# Revit family: 54-3132-001 DN1400-1800
name_source: partatom
category: Pipe Accessories
units: mm (PartAtom-declared; Revit-internal decimal feet)

## family parameters
Always vertical = No
Cut with Voids When Loaded = No
Part Type = Valve - Breaks Into
Round Connector Dimension = Use Diameter
Shared = No
Work Plane-Based = No

## types (19) — shared parameters
1 = 1 mm  [stored 0.00328084 ft]
10 = 10 mm  [stored 0.0328084 ft]
54-1400-31-0303100 = DN1400_ PN10_ CTC
54-1400-31-0304100 = DN1400_ PN10_ CTC
54-1400-31-1303100 = DN1400_ PN16_ CTC
54-1400-31-1304100 = DN1400_ PN16_ CTC
54-1400-32-0303100 = DN1400_ PN10_ CTO
54-1400-32-1303100 = DN1400_ PN16_ CTO
54-1400-32-1304100 = DN1400_ PN16_ CTO
54-1500-31-0304100 = DN1500_ PN10_ CTC
54-1500-31-1304100 = DN1500_ PN16_ CTC
54-1600-31-0303100 = DN1600_ PN10_ CTC
54-1600-31-0304100 = DN1600_ PN10_ CTC
54-1600-31-1303100 = DN1600_ PN16_ CTC
54-1600-31-1304100 = DN1600_ PN16_ CTC
54-1600-32-0303100 = DN1600_ PN10_ CTO
54-1600-32-1303100 = DN1600_ PN16_ CTO
54-1800-31-0304100 = DN1800_ PN10_ CTC
54-1800-31-1304100 = DN1800_ PN16_ CTC
54-1800-32-0304100 = DN1800_ PN10_ CTO
54-1800-32-1304100 = DN1800_ PN16_ CTO
Bypass_W = 82 mm
Bypass_dis = 60 mm
Description_ = AVK METAL SEAT GATE VALVE, FLANGED, PN 10/16
H = 782 mm
Raised_dis = 5 mm  [stored 0.0164042 ft]
Rib_H1 = 300 mm
Search_table = 54-3132-001 DN1400-1800
URL product pages = https://www.avkvalves.com
sweep = 6 mm  [stored 0.019685 ft]
zero-valued in all types: Default Elevation

## per-type parameters (varying)
- 54-1400-31-0303100: ACtuator_T=33.12 mm  [stored 0.108661 ft]; ADN=1400 mm; Actuator_FLR=150 mm; Actuator_angle=133.41 mm; Actuator_dim1=90 mm; Actuator_dim2=54 mm  [stored 0.177165 ft]; BP_centre=31 mm  [stored 0.101706 ft]; Body_H=1435 mm; Body_L=1564.8 mm; Body_T=692.5 mm; Body_W=648 mm; Body_rib_T=18.4 mm  [stored 0.0603675 ft]; Bonnet_FL_L=1956 mm; Bonnet_FL_T=87.4 mm; Bonnet_FL_W=864 mm; Bonnet_dim1=312.96 mm; Bonnet_dim2=226.8 mm; Bonnet_dim3=2468.2 mm; Bonnet_fillet=72 mm; Bore=700 mm; Bypass_Arc=85 mm; Bypass_Location=220 mm; Bypass_R=62 mm; Bypass_R1=124 mm; Bypass_T=25 mm  [stored 0.082021 ft]; Bypass_shaft=150 mm; Cut_dis=43.7 mm  [stored 0.143373 ft]; DN=1400 mm; F=60 mm; F1=27 mm  [stored 0.0885827 ft]; F2=166 mm; FL_T=46 mm  [stored 0.150919 ft]; Fillet=216 mm; H1=2870 mm; H2=885 mm; L=876 mm; OD=1770 mm; OD1=1770 mm; PN=10 mm  [stored 0.0328084 ft]; Raised_dia=1530 mm; Rib_Actual=978 mm; Rib_H=1148 mm; Rib_H2=950 mm; Rib_H3=1200 mm; Rib_H4=1310 mm; Rib_L=880.2 mm; Rib_W=388.8 mm; Stem_dim=75 mm; W=1956 mm; W1=897 mm; W_half=1059 mm; bottom_rib=885 mm; stem_dim=55.33 mm; stem_dim1=97.5 mm; wedge_dim1=712.8 mm
- 54-1400-31-0304100: ACtuator_T=33.12 mm  [stored 0.108661 ft]; ADN=1400 mm; Actuator_FLR=175 mm; Actuator_angle=133.41 mm; Actuator_dim1=105 mm; Actuator_dim2=63 mm; BP_centre=31 mm  [stored 0.101706 ft]; Body_H=1435 mm; Body_L=1564.8 mm; Body_T=692.5 mm; Body_W=648 mm; Body_rib_T=18.4 mm  [stored 0.0603675 ft]; Bonnet_FL_L=1956 mm; Bonnet_FL_T=87.4 mm; Bonnet_FL_W=864 mm; Bonnet_dim1=312.96 mm; Bonnet_dim2=226.8 mm; Bonnet_dim3=2468.2 mm; Bonnet_fillet=72 mm; Bore=700.05 mm; Bypass_Arc=85 mm; Bypass_Location=220 mm; Bypass_R=62 mm; Bypass_R1=124 mm; Bypass_T=25 mm  [stored 0.082021 ft]; Bypass_shaft=150 mm; Cut_dis=43.7 mm  [stored 0.143373 ft]; DN=1400.1 mm; F=70 mm; F1=31.5 mm  [stored 0.103346 ft]; F2=202 mm; FL_T=46 mm  [stored 0.150919 ft]; Fillet=216 mm; H1=2870 mm; H2=885 mm; L=876 mm; OD=1770 mm; OD1=1770 mm; PN=10 mm  [stored 0.0328084 ft]; Raised_dia=1530 mm; Rib_Actual=978 mm; Rib_H=1148 mm; Rib_H2=950 mm; Rib_H3=1200 mm; Rib_H4=1310 mm; Rib_L=880.2 mm; Rib_W=388.8 mm; Stem_dim=87.5 mm; W=1956 mm; W1=897 mm; W_half=1059 mm; bottom_rib=885 mm; stem_dim=67.33 mm; stem_dim1=113.75 mm; wedge_dim1=712.8 mm
- 54-1400-31-1303100: ACtuator_T=43.2 mm  [stored 0.141732 ft]; ADN=1400 mm; Actuator_FLR=150 mm; Actuator_angle=133.41 mm; Actuator_dim1=90 mm; Actuator_dim2=54 mm  [stored 0.177165 ft]; BP_centre=31 mm  [stored 0.101706 ft]; Body_H=1435 mm; Body_L=1564.8 mm; Body_T=692.5 mm; Body_W=648 mm; Body_rib_T=24 mm  [stored 0.0787402 ft]; Bonnet_FL_L=1956 mm; Bonnet_FL_T=114 mm; Bonnet_FL_W=864 mm; Bonnet_dim1=312.96 mm; Bonnet_dim2=226.8 mm; Bonnet_dim3=2468.2 mm; Bonnet_fillet=72 mm; Bore=700.06 mm; Bypass_Arc=85 mm; Bypass_Location=220 mm; Bypass_R=62 mm; Bypass_R1=124 mm; Bypass_T=25 mm  [stored 0.082021 ft]; Bypass_shaft=150 mm; Cut_dis=57 mm; DN=1400.11 mm; F=60 mm; F1=27 mm  [stored 0.0885827 ft]; F2=166 mm; FL_T=60 mm; Fillet=216 mm; H1=2870 mm; H2=885 mm; L=876 mm; OD=1770 mm; OD1=1770 mm; PN=16 mm  [stored 0.0524934 ft]; Raised_dia=1530 mm; Rib_Actual=978 mm; Rib_H=1148 mm; Rib_H2=950 mm; Rib_H3=1200 mm; Rib_H4=1310 mm; Rib_L=880.2 mm; Rib_W=388.8 mm; Stem_dim=75 mm; W=1956 mm; W1=897 mm; W_half=1059 mm; bottom_rib=885 mm; stem_dim=55.33 mm; stem_dim1=97.5 mm; wedge_dim1=712.8 mm
- 54-1400-31-1304100: ACtuator_T=43.2 mm  [stored 0.141732 ft]; ADN=1400 mm; Actuator_FLR=175 mm; Actuator_angle=133.41 mm; Actuator_dim1=105 mm; Actuator_dim2=63 mm; BP_centre=31 mm  [stored 0.101706 ft]; Body_H=1435 mm; Body_L=1564.8 mm; Body_T=692.5 mm; Body_W=648 mm; Body_rib_T=24 mm  [stored 0.0787402 ft]; Bonnet_FL_L=1956 mm; Bonnet_FL_T=114 mm; Bonnet_FL_W=864 mm; Bonnet_dim1=312.96 mm; Bonnet_dim2=226.8 mm; Bonnet_dim3=2468.2 mm; Bonnet_fillet=72 mm; Bore=700.06 mm; Bypass_Arc=85 mm; Bypass_Location=220 mm; Bypass_R=62 mm; Bypass_R1=124 mm; Bypass_T=25 mm  [stored 0.082021 ft]; Bypass_shaft=150 mm; Cut_dis=57 mm; DN=1400.12 mm; F=70 mm; F1=31.5 mm  [stored 0.103346 ft]; F2=202 mm; FL_T=60 mm; Fillet=216 mm; H1=2870 mm; H2=885 mm; L=876 mm; OD=1770 mm; OD1=1770 mm; PN=16 mm  [stored 0.0524934 ft]; Raised_dia=1530 mm; Rib_Actual=978 mm; Rib_H=1148 mm; Rib_H2=950 mm; Rib_H3=1200 mm; Rib_H4=1310 mm; Rib_L=880.2 mm; Rib_W=388.8 mm; Stem_dim=87.5 mm; W=1956 mm; W1=897 mm; W_half=1059 mm; bottom_rib=885 mm; stem_dim=67.33 mm; stem_dim1=113.75 mm; wedge_dim1=712.8 mm
- 54-1400-32-0303100: ACtuator_T=33.12 mm  [stored 0.108661 ft]; ADN=1400 mm; Actuator_FLR=150 mm; Actuator_angle=133.41 mm; Actuator_dim1=90 mm; Actuator_dim2=54 mm  [stored 0.177165 ft]; BP_centre=31 mm  [stored 0.101706 ft]; Body_H=1435 mm; Body_L=1564.8 mm; Body_T=692.5 mm; Body_W=648 mm; Body_rib_T=18.4 mm  [stored 0.0603675 ft]; Bonnet_FL_L=1956 mm; Bonnet_FL_T=87.4 mm; Bonnet_FL_W=864 mm; Bonnet_dim1=312.96 mm; Bonnet_dim2=226.8 mm; Bonnet_dim3=2468.2 mm; Bonnet_fillet=72 mm; Bore=700.07 mm; Bypass_Arc=85 mm; Bypass_Location=220 mm; Bypass_R=62 mm; Bypass_R1=124 mm; Bypass_T=25 mm  [stored 0.082021 ft]; Bypass_shaft=150 mm; Cut_dis=43.7 mm  [stored 0.143373 ft]; DN=1400.13 mm; F=60 mm; F1=27 mm  [stored 0.0885827 ft]; F2=166 mm; FL_T=46 mm  [stored 0.150919 ft]; Fillet=216 mm; H1=2870 mm; H2=885 mm; L=876 mm; OD=1770 mm; OD1=1770 mm; PN=10 mm  [stored 0.0328084 ft]; Raised_dia=1530 mm; Rib_Actual=978 mm; Rib_H=1148 mm; Rib_H2=950 mm; Rib_H3=1200 mm; Rib_H4=1310 mm; Rib_L=880.2 mm; Rib_W=388.8 mm; Stem_dim=75 mm; W=1956 mm; W1=897 mm; W_half=1059 mm; bottom_rib=885 mm; stem_dim=55.33 mm; stem_dim1=97.5 mm; wedge_dim1=712.8 mm
- 54-1400-32-1303100: ACtuator_T=43.2 mm  [stored 0.141732 ft]; ADN=1400 mm; Actuator_FLR=150 mm; Actuator_angle=133.41 mm; Actuator_dim1=90 mm; Actuator_dim2=54 mm  [stored 0.177165 ft]; BP_centre=31 mm  [stored 0.101706 ft]; Body_H=1435 mm; Body_L=1564.8 mm; Body_T=692.5 mm; Body_W=648 mm; Body_rib_T=24 mm  [stored 0.0787402 ft]; Bonnet_FL_L=1956 mm; Bonnet_FL_T=114 mm; Bonnet_FL_W=864 mm; Bonnet_dim1=312.96 mm; Bonnet_dim2=226.8 mm; Bonnet_dim3=2468.2 mm; Bonnet_fillet=72 mm; Bore=700.07 mm; Bypass_Arc=85 mm; Bypass_Location=220 mm; Bypass_R=62 mm; Bypass_R1=124 mm; Bypass_T=25 mm  [stored 0.082021 ft]; Bypass_shaft=150 mm; Cut_dis=57 mm; DN=1400.14 mm; F=60 mm; F1=27 mm  [stored 0.0885827 ft]; F2=166 mm; FL_T=60 mm; Fillet=216 mm; H1=2870 mm; H2=885 mm; L=876 mm; OD=1770 mm; OD1=1770 mm; PN=16 mm  [stored 0.0524934 ft]; Raised_dia=1530 mm; Rib_Actual=978 mm; Rib_H=1148 mm; Rib_H2=950 mm; Rib_H3=1200 mm; Rib_H4=1310 mm; Rib_L=880.2 mm; Rib_W=388.8 mm; Stem_dim=75 mm; W=1956 mm; W1=897 mm; W_half=1059 mm; bottom_rib=885 mm; stem_dim=55.33 mm; stem_dim1=97.5 mm; wedge_dim1=712.8 mm
- 54-1400-32-1304100: ACtuator_T=43.2 mm  [stored 0.141732 ft]; ADN=1400 mm; Actuator_FLR=175 mm; Actuator_angle=133.41 mm; Actuator_dim1=105 mm; Actuator_dim2=63 mm; BP_centre=31 mm  [stored 0.101706 ft]; Body_H=1435 mm; Body_L=1564.8 mm; Body_T=692.5 mm; Body_W=648 mm; Body_rib_T=24 mm  [stored 0.0787402 ft]; Bonnet_FL_L=1956 mm; Bonnet_FL_T=114 mm; Bonnet_FL_W=864 mm; Bonnet_dim1=312.96 mm; Bonnet_dim2=226.8 mm; Bonnet_dim3=2468.2 mm; Bonnet_fillet=72 mm; Bore=700.08 mm; Bypass_Arc=85 mm; Bypass_Location=220 mm; Bypass_R=62 mm; Bypass_R1=124 mm; Bypass_T=25 mm  [stored 0.082021 ft]; Bypass_shaft=150 mm; Cut_dis=57 mm; DN=1400.15 mm; F=70 mm; F1=31.5 mm  [stored 0.103346 ft]; F2=202 mm; FL_T=60 mm; Fillet=216 mm; H1=2870 mm; H2=885 mm; L=876 mm; OD=1770 mm; OD1=1770 mm; PN=16 mm  [stored 0.0524934 ft]; Raised_dia=1530 mm; Rib_Actual=978 mm; Rib_H=1148 mm; Rib_H2=950 mm; Rib_H3=1200 mm; Rib_H4=1310 mm; Rib_L=880.2 mm; Rib_W=388.8 mm; Stem_dim=87.5 mm; W=1956 mm; W1=897 mm; W_half=1059 mm; bottom_rib=885 mm; stem_dim=67.33 mm; stem_dim1=113.75 mm; wedge_dim1=712.8 mm
- 54-1500-31-0304100: ACtuator_T=34.2 mm  [stored 0.112205 ft]; ADN=1500 mm; Actuator_FLR=175 mm; Actuator_angle=141.13 mm; Actuator_dim1=105 mm; Actuator_dim2=63 mm; BP_centre=37.5 mm; Body_H=1584.5 mm; Body_L=1768 mm; Body_T=742.5 mm; Body_W=685.5 mm; Body_rib_T=19 mm  [stored 0.062336 ft]; Bonnet_FL_L=2210 mm; Bonnet_FL_T=90.25 mm; Bonnet_FL_W=914 mm; Bonnet_dim1=353.6 mm; Bonnet_dim2=239.93 mm; Bonnet_dim3=2725.34 mm; Bonnet_fillet=76.17 mm; Bore=750 mm; Bypass_Arc=85 mm; Bypass_Location=220 mm; Bypass_R=75 mm; Bypass_R1=150 mm; Bypass_T=18 mm  [stored 0.0590551 ft]; Bypass_shaft=160 mm; Cut_dis=45.13 mm; DN=1500 mm; F=70 mm; F1=31.5 mm  [stored 0.103346 ft]; F2=205 mm; FL_T=47.5 mm; Fillet=228.5 mm; H1=3169 mm; H2=1016 mm; L=914 mm; OD=2032 mm; OD1=2032 mm; PN=10 mm  [stored 0.0328084 ft]; Raised_dia=1640 mm; Rib_Actual=1105 mm; Rib_H=1267.6 mm; Rib_H2=1200 mm; Rib_H3=1300 mm; Rib_H4=1450 mm; Rib_L=994.5 mm; Rib_W=411.3 mm; Stem_dim=87.5 mm; W=2210 mm; W1=1000 mm; W_half=1210 mm; bottom_rib=1016 mm; stem_dim=68.33 mm; stem_dim1=113.75 mm; wedge_dim1=754.05 mm
- 54-1500-31-1304100: ACtuator_T=45 mm  [stored 0.147638 ft]; ADN=1500 mm; Actuator_FLR=175 mm; Actuator_angle=141.13 mm; Actuator_dim1=105 mm; Actuator_dim2=63 mm; BP_centre=37.5 mm; Body_H=1584.5 mm; Body_L=1768 mm; Body_T=742.5 mm; Body_W=685.5 mm; Body_rib_T=25 mm  [stored 0.082021 ft]; Bonnet_FL_L=2210 mm; Bonnet_FL_T=118.75 mm; Bonnet_FL_W=914 mm; Bonnet_dim1=353.6 mm; Bonnet_dim2=239.93 mm; Bonnet_dim3=2725.34 mm; Bonnet_fillet=76.17 mm; Bore=750.05 mm; Bypass_Arc=85 mm; Bypass_Location=220 mm; Bypass_R=75 mm; Bypass_R1=150 mm; Bypass_T=18 mm  [stored 0.0590551 ft]; Bypass_shaft=160 mm; Cut_dis=59.38 mm; DN=1500.1 mm; F=70 mm; F1=31.5 mm  [stored 0.103346 ft]; F2=205 mm; FL_T=62.5 mm; Fillet=228.5 mm; H1=3169 mm; H2=1016 mm; L=914 mm; OD=2032 mm; OD1=2032 mm; PN=16 mm  [stored 0.0524934 ft]; Raised_dia=1640 mm; Rib_Actual=1105 mm; Rib_H=1267.6 mm; Rib_H2=1200 mm; Rib_H3=1300 mm; Rib_H4=1450 mm; Rib_L=994.5 mm; Rib_W=411.3 mm; Stem_dim=87.5 mm; W=2210 mm; W1=1000 mm; W_half=1210 mm; bottom_rib=1016 mm; stem_dim=68.33 mm; stem_dim1=113.75 mm; wedge_dim1=754.05 mm
- 54-1600-31-0303100: ACtuator_T=35.28 mm  [stored 0.115748 ft]; ADN=1600 mm; Actuator_FLR=150 mm; Actuator_angle=141.13 mm; Actuator_dim1=90 mm; Actuator_dim2=54 mm  [stored 0.177165 ft]; BP_centre=40 mm  [stored 0.131234 ft]; Body_H=1645.5 mm; Body_L=1832 mm; Body_T=792.5 mm; Body_W=685.5 mm; Body_rib_T=19.6 mm  [stored 0.0643045 ft]; Bonnet_FL_L=2290 mm; Bonnet_FL_T=93.1 mm; Bonnet_FL_W=914 mm; Bonnet_dim1=366.4 mm; Bonnet_dim2=239.93 mm; Bonnet_dim3=2830.26 mm; Bonnet_fillet=76.17 mm; Bore=800 mm; Bypass_Arc=100 mm; Bypass_Location=259 mm; Bypass_R=80 mm; Bypass_R1=160 mm; Bypass_T=35 mm  [stored 0.114829 ft]; Bypass_shaft=170 mm; Cut_dis=46.55 mm  [stored 0.152723 ft]; DN=1600 mm; F=60 mm; F1=27 mm  [stored 0.0885827 ft]; F2=179 mm; FL_T=49 mm  [stored 0.160761 ft]; Fillet=228.5 mm; H1=3291 mm; H2=1060 mm; L=914 mm; OD=2120 mm; OD1=2120 mm; PN=10 mm  [stored 0.0328084 ft]; Raised_dia=1750 mm; Rib_Actual=1145 mm; Rib_H=1316.4 mm; Rib_H2=1100 mm; Rib_H3=1300 mm; Rib_H4=1500 mm; Rib_L=1030.5 mm; Rib_W=411.3 mm; Stem_dim=75 mm; W=2290 mm; W1=1104 mm; W_half=1186 mm; bottom_rib=1060 mm; stem_dim=59.67 mm; stem_dim1=97.5 mm; wedge_dim1=754.05 mm
- 54-1600-31-0304100: ACtuator_T=35.28 mm  [stored 0.115748 ft]; ADN=1600 mm; Actuator_FLR=175 mm; Actuator_angle=141.13 mm; Actuator_dim1=105 mm; Actuator_dim2=63 mm; BP_centre=40 mm  [stored 0.131234 ft]; Body_H=1645.5 mm; Body_L=1832 mm; Body_T=792.5 mm; Body_W=685.5 mm; Body_rib_T=19.6 mm  [stored 0.0643045 ft]; Bonnet_FL_L=2290 mm; Bonnet_FL_T=93.1 mm; Bonnet_FL_W=914 mm; Bonnet_dim1=366.4 mm; Bonnet_dim2=239.93 mm; Bonnet_dim3=2830.26 mm; Bonnet_fillet=76.17 mm; Bore=800.05 mm; Bypass_Arc=100 mm; Bypass_Location=259 mm; Bypass_R=80 mm; Bypass_R1=160 mm; Bypass_T=35 mm  [stored 0.114829 ft]; Bypass_shaft=170 mm; Cut_dis=46.55 mm  [stored 0.152723 ft]; DN=1600.1 mm; F=70 mm; F1=31.5 mm  [stored 0.103346 ft]; F2=205 mm; FL_T=49 mm  [stored 0.160761 ft]; Fillet=228.5 mm; H1=3291 mm; H2=1060 mm; L=914 mm; OD=2120 mm; OD1=2120 mm; PN=10 mm  [stored 0.0328084 ft]; Raised_dia=1750 mm; Rib_Actual=1145 mm; Rib_H=1316.4 mm; Rib_H2=1100 mm; Rib_H3=1300 mm; Rib_H4=1500 mm; Rib_L=1030.5 mm; Rib_W=411.3 mm; Stem_dim=87.5 mm; W=2290 mm; W1=1104 mm; W_half=1186 mm; bottom_rib=1060 mm; stem_dim=68.33 mm; stem_dim1=113.75 mm; wedge_dim1=754.05 mm
- 54-1600-31-1303100: ACtuator_T=46.8 mm  [stored 0.153543 ft]; ADN=1600 mm; Actuator_FLR=150 mm; Actuator_angle=141.13 mm; Actuator_dim1=90 mm; Actuator_dim2=54 mm  [stored 0.177165 ft]; BP_centre=40 mm  [stored 0.131234 ft]; Body_H=1645.5 mm; Body_L=1832 mm; Body_T=792.5 mm; Body_W=685.5 mm; Body_rib_T=26 mm; Bonnet_FL_L=2290 mm; Bonnet_FL_T=123.5 mm; Bonnet_FL_W=914 mm; Bonnet_dim1=366.4 mm; Bonnet_dim2=239.93 mm; Bonnet_dim3=2830.26 mm; Bonnet_fillet=76.17 mm; Bore=800.06 mm; Bypass_Arc=100 mm; Bypass_Location=259 mm; Bypass_R=80 mm; Bypass_R1=160 mm; Bypass_T=35 mm  [stored 0.114829 ft]; Bypass_shaft=170 mm; Cut_dis=61.75 mm; DN=1600.11 mm; F=60 mm; F1=27 mm  [stored 0.0885827 ft]; F2=179 mm; FL_T=65 mm; Fillet=228.5 mm; H1=3291 mm; H2=1060 mm; L=914 mm; OD=2120 mm; OD1=2120 mm; PN=16 mm  [stored 0.0524934 ft]; Raised_dia=1750 mm; Rib_Actual=1145 mm; Rib_H=1316.4 mm; Rib_H2=1100 mm; Rib_H3=1300 mm; Rib_H4=1500 mm; Rib_L=1030.5 mm; Rib_W=411.3 mm; Stem_dim=75 mm; W=2290 mm; W1=1104 mm; W_half=1186 mm; bottom_rib=1060 mm; stem_dim=59.67 mm; stem_dim1=97.5 mm; wedge_dim1=754.05 mm
- 54-1600-31-1304100: ACtuator_T=46.8 mm  [stored 0.153543 ft]; ADN=1600 mm; Actuator_FLR=175 mm; Actuator_angle=141.13 mm; Actuator_dim1=105 mm; Actuator_dim2=63 mm; BP_centre=40 mm  [stored 0.131234 ft]; Body_H=1645.5 mm; Body_L=1832 mm; Body_T=792.5 mm; Body_W=685.5 mm; Body_rib_T=26 mm; Bonnet_FL_L=2290 mm; Bonnet_FL_T=123.5 mm; Bonnet_FL_W=914 mm; Bonnet_dim1=366.4 mm; Bonnet_dim2=239.93 mm; Bonnet_dim3=2830.26 mm; Bonnet_fillet=76.17 mm; Bore=800.06 mm; Bypass_Arc=100 mm; Bypass_Location=259 mm; Bypass_R=80 mm; Bypass_R1=160 mm; Bypass_T=35 mm  [stored 0.114829 ft]; Bypass_shaft=170 mm; Cut_dis=61.75 mm; DN=1600.12 mm; F=70 mm; F1=31.5 mm  [stored 0.103346 ft]; F2=205 mm; FL_T=65 mm; Fillet=228.5 mm; H1=3291 mm; H2=1060 mm; L=914 mm; OD=2120 mm; OD1=2120 mm; PN=16 mm  [stored 0.0524934 ft]; Raised_dia=1750 mm; Rib_Actual=1145 mm; Rib_H=1316.4 mm; Rib_H2=1100 mm; Rib_H3=1300 mm; Rib_H4=1500 mm; Rib_L=1030.5 mm; Rib_W=411.3 mm; Stem_dim=87.5 mm; W=2290 mm; W1=1104 mm; W_half=1186 mm; bottom_rib=1060 mm; stem_dim=68.33 mm; stem_dim1=113.75 mm; wedge_dim1=754.05 mm
- 54-1600-32-0303100: ACtuator_T=35.28 mm  [stored 0.115748 ft]; ADN=1600 mm; Actuator_FLR=150 mm; Actuator_angle=141.13 mm; Actuator_dim1=90 mm; Actuator_dim2=54 mm  [stored 0.177165 ft]; BP_centre=40 mm  [stored 0.131234 ft]; Body_H=1645.5 mm; Body_L=1832 mm; Body_T=792.5 mm; Body_W=685.5 mm; Body_rib_T=19.6 mm  [stored 0.0643045 ft]; Bonnet_FL_L=2290 mm; Bonnet_FL_T=93.1 mm; Bonnet_FL_W=914 mm; Bonnet_dim1=366.4 mm; Bonnet_dim2=239.93 mm; Bonnet_dim3=2830.26 mm; Bonnet_fillet=76.17 mm; Bore=800.07 mm; Bypass_Arc=100 mm; Bypass_Location=259 mm; Bypass_R=80 mm; Bypass_R1=160 mm; Bypass_T=35 mm  [stored 0.114829 ft]; Bypass_shaft=170 mm; Cut_dis=46.55 mm  [stored 0.152723 ft]; DN=1600.13 mm; F=60 mm; F1=27 mm  [stored 0.0885827 ft]; F2=179 mm; FL_T=49 mm  [stored 0.160761 ft]; Fillet=228.5 mm; H1=3291 mm; H2=1060 mm; L=914 mm; OD=2120 mm; OD1=2120 mm; PN=10 mm  [stored 0.0328084 ft]; Raised_dia=1750 mm; Rib_Actual=1145 mm; Rib_H=1316.4 mm; Rib_H2=1100 mm; Rib_H3=1300 mm; Rib_H4=1500 mm; Rib_L=1030.5 mm; Rib_W=411.3 mm; Stem_dim=75 mm; W=2290 mm; W1=1104 mm; W_half=1186 mm; bottom_rib=1060 mm; stem_dim=59.67 mm; stem_dim1=97.5 mm; wedge_dim1=754.05 mm
- 54-1600-32-1303100: ACtuator_T=46.8 mm  [stored 0.153543 ft]; ADN=1600 mm; Actuator_FLR=150 mm; Actuator_angle=141.13 mm; Actuator_dim1=90 mm; Actuator_dim2=54 mm  [stored 0.177165 ft]; BP_centre=40 mm  [stored 0.131234 ft]; Body_H=1645.5 mm; Body_L=1832 mm; Body_T=792.5 mm; Body_W=685.5 mm; Body_rib_T=26 mm; Bonnet_FL_L=2290 mm; Bonnet_FL_T=123.5 mm; Bonnet_FL_W=914 mm; Bonnet_dim1=366.4 mm; Bonnet_dim2=239.93 mm; Bonnet_dim3=2830.26 mm; Bonnet_fillet=76.17 mm; Bore=800.07 mm; Bypass_Arc=100 mm; Bypass_Location=259 mm; Bypass_R=80 mm; Bypass_R1=160 mm; Bypass_T=35 mm  [stored 0.114829 ft]; Bypass_shaft=170 mm; Cut_dis=61.75 mm; DN=1600.14 mm; F=60 mm; F1=27 mm  [stored 0.0885827 ft]; F2=179 mm; FL_T=65 mm; Fillet=228.5 mm; H1=3291 mm; H2=1060 mm; L=914 mm; OD=2120 mm; OD1=2120 mm; PN=16 mm  [stored 0.0524934 ft]; Raised_dia=1750 mm; Rib_Actual=1145 mm; Rib_H=1316.4 mm; Rib_H2=1100 mm; Rib_H3=1300 mm; Rib_H4=1500 mm; Rib_L=1030.5 mm; Rib_W=411.3 mm; Stem_dim=75 mm; W=2290 mm; W1=1104 mm; W_half=1186 mm; bottom_rib=1060 mm; stem_dim=59.67 mm; stem_dim1=97.5 mm; wedge_dim1=754.05 mm
- 54-1800-31-0304100: ACtuator_T=37.44 mm  [stored 0.122835 ft]; ADN=1800 mm; Actuator_FLR=175 mm; Actuator_angle=156.88 mm; Actuator_dim1=105 mm; Actuator_dim2=63 mm; BP_centre=42.5 mm  [stored 0.139436 ft]; Body_H=1829.5 mm; Body_L=1910.4 mm; Body_T=892.5 mm; Body_W=762 mm; Body_rib_T=20.8 mm  [stored 0.0682415 ft]; Bonnet_FL_L=2388 mm; Bonnet_FL_T=98.8 mm; Bonnet_FL_W=1016 mm; Bonnet_dim1=382.08 mm; Bonnet_dim2=266.7 mm; Bonnet_dim3=3146.74 mm; Bonnet_fillet=84.67 mm; Bore=900 mm; Bypass_Arc=105 mm; Bypass_Location=259 mm; Bypass_R=85 mm; Bypass_R1=170 mm; Bypass_T=40 mm  [stored 0.131234 ft]; Bypass_shaft=150 mm; Cut_dis=49.4 mm  [stored 0.162073 ft]; DN=1800 mm; F=70 mm; F1=31.5 mm  [stored 0.103346 ft]; F2=208 mm; FL_T=52 mm; Fillet=254 mm; H1=3659 mm; H2=1180 mm; L=1067 mm; OD=2360 mm; OD1=2360 mm; PN=10 mm  [stored 0.0328084 ft]; Raised_dia=1950 mm; Rib_Actual=1227 mm; Rib_H=1463.6 mm; Rib_H2=1300 mm; Rib_H3=1500 mm; Rib_H4=1700 mm; Rib_L=1074.6 mm; Rib_W=457.2 mm; Stem_dim=87.5 mm; W=2454 mm; W1=1260 mm; W_half=1194 mm; bottom_rib=1180 mm; stem_dim=69.33 mm; stem_dim1=113.75 mm; wedge_dim1=838.2 mm
- 54-1800-31-1304100: ACtuator_T=50.4 mm  [stored 0.165354 ft]; ADN=1800 mm; Actuator_FLR=175 mm; Actuator_angle=156.88 mm; Actuator_dim1=105 mm; Actuator_dim2=63 mm; BP_centre=42.5 mm  [stored 0.139436 ft]; Body_H=1829.5 mm; Body_L=1910.4 mm; Body_T=892.5 mm; Body_W=762 mm; Body_rib_T=28 mm  [stored 0.0918635 ft]; Bonnet_FL_L=2388 mm; Bonnet_FL_T=133 mm; Bonnet_FL_W=1016 mm; Bonnet_dim1=382.08 mm; Bonnet_dim2=266.7 mm; Bonnet_dim3=3146.74 mm; Bonnet_fillet=84.67 mm; Bore=900.05 mm; Bypass_Arc=105 mm; Bypass_Location=259 mm; Bypass_R=85 mm; Bypass_R1=170 mm; Bypass_T=40 mm  [stored 0.131234 ft]; Bypass_shaft=150 mm; Cut_dis=66.5 mm; DN=1800.1 mm; F=70 mm; F1=31.5 mm  [stored 0.103346 ft]; F2=208 mm; FL_T=70 mm; Fillet=254 mm; H1=3659 mm; H2=1180 mm; L=1067 mm; OD=2360 mm; OD1=2360 mm; PN=16 mm  [stored 0.0524934 ft]; Raised_dia=1950 mm; Rib_Actual=1227 mm; Rib_H=1463.6 mm; Rib_H2=1300 mm; Rib_H3=1500 mm; Rib_H4=1700 mm; Rib_L=1074.6 mm; Rib_W=457.2 mm; Stem_dim=87.5 mm; W=2454 mm; W1=1260 mm; W_half=1194 mm; bottom_rib=1180 mm; stem_dim=69.33 mm; stem_dim1=113.75 mm; wedge_dim1=838.2 mm
- 54-1800-32-0304100: ACtuator_T=37.44 mm  [stored 0.122835 ft]; ADN=1800 mm; Actuator_FLR=175 mm; Actuator_angle=156.88 mm; Actuator_dim1=105 mm; Actuator_dim2=63 mm; BP_centre=42.5 mm  [stored 0.139436 ft]; Body_H=1829.5 mm; Body_L=1910.4 mm; Body_T=892.5 mm; Body_W=762 mm; Body_rib_T=20.8 mm  [stored 0.0682415 ft]; Bonnet_FL_L=2388 mm; Bonnet_FL_T=98.8 mm; Bonnet_FL_W=1016 mm; Bonnet_dim1=382.08 mm; Bonnet_dim2=266.7 mm; Bonnet_dim3=3146.74 mm; Bonnet_fillet=84.67 mm; Bore=900.06 mm; Bypass_Arc=105 mm; Bypass_Location=259 mm; Bypass_R=85 mm; Bypass_R1=170 mm; Bypass_T=40 mm  [stored 0.131234 ft]; Bypass_shaft=150 mm; Cut_dis=49.4 mm  [stored 0.162073 ft]; DN=1800.11 mm; F=70 mm; F1=31.5 mm  [stored 0.103346 ft]; F2=208 mm; FL_T=52 mm; Fillet=254 mm; H1=3659 mm; H2=1180 mm; L=1067 mm; OD=2360 mm; OD1=2360 mm; PN=10 mm  [stored 0.0328084 ft]; Raised_dia=1950 mm; Rib_Actual=1227 mm; Rib_H=1463.6 mm; Rib_H2=1300 mm; Rib_H3=1500 mm; Rib_H4=1700 mm; Rib_L=1074.6 mm; Rib_W=457.2 mm; Stem_dim=87.5 mm; W=2454 mm; W1=1260 mm; W_half=1194 mm; bottom_rib=1180 mm; stem_dim=69.33 mm; stem_dim1=113.75 mm; wedge_dim1=838.2 mm
- 54-1800-32-1304100: ACtuator_T=50.4 mm  [stored 0.165354 ft]; ADN=1800 mm; Actuator_FLR=175 mm; Actuator_angle=156.88 mm; Actuator_dim1=105 mm; Actuator_dim2=63 mm; BP_centre=42.5 mm  [stored 0.139436 ft]; Body_H=1829.5 mm; Body_L=1910.4 mm; Body_T=892.5 mm; Body_W=762 mm; Body_rib_T=28 mm  [stored 0.0918635 ft]; Bonnet_FL_L=2388 mm; Bonnet_FL_T=133 mm; Bonnet_FL_W=1016 mm; Bonnet_dim1=382.08 mm; Bonnet_dim2=266.7 mm; Bonnet_dim3=3146.74 mm; Bonnet_fillet=84.67 mm; Bore=900.06 mm; Bypass_Arc=105 mm; Bypass_Location=259 mm; Bypass_R=85 mm; Bypass_R1=170 mm; Bypass_T=40 mm  [stored 0.131234 ft]; Bypass_shaft=150 mm; Cut_dis=66.5 mm; DN=1800.12 mm; F=70 mm; F1=31.5 mm  [stored 0.103346 ft]; F2=208 mm; FL_T=70 mm; Fillet=254 mm; H1=3659 mm; H2=1180 mm; L=1067 mm; OD=2360 mm; OD1=2360 mm; PN=16 mm  [stored 0.0524934 ft]; Raised_dia=1950 mm; Rib_Actual=1227 mm; Rib_H=1463.6 mm; Rib_H2=1300 mm; Rib_H3=1500 mm; Rib_H4=1700 mm; Rib_L=1074.6 mm; Rib_W=457.2 mm; Stem_dim=87.5 mm; W=2454 mm; W1=1260 mm; W_half=1194 mm; bottom_rib=1180 mm; stem_dim=69.33 mm; stem_dim1=113.75 mm; wedge_dim1=838.2 mm

note: [stored X ft] marks values corroborated as IEEE doubles in the binary element streams (Revit-internal decimal feet)

## geometry (parser evidence)
native form markers: Sweep x4
no freeform markers — native parametric forms only
